# Revit family: Building-IEC309Connections-GEWISS-IEC309HP-10°_FLUSH-MOUNT_SOCKET_32A_IP44-54
name_source: partatom
category: Apparecchi elettrici
units: mm (PartAtom-declared; Revit-internal decimal feet)

## family parameters
Condiviso = Sì
Host = Superficie
Mantenere orientamento annotazione = Sì
Punto di calcolo locali = Sì
Quota connettore circolare = Usa diametro
Taglio con vuoti quando caricato = No
Tipo di parte = Normale

## types (28) — shared parameters
Breaking capacity at 1.1 Un = 40A
Catalogue = BUILDING
Corpo centrale = Default(2)
FORMULA = 1000 mm  [stored 3.28084 ft]
Flange dimensions (mm) = 95x80
Glow wire test: = 850 °C (active parts) - 650 °C (passive parts)
IDF = e593e5aa-3fae-48bf-b1cb-87c0f69a9db0
IDT = b8406758f3304951a22d0997e08313ec
IP degree = IP44/IP54
Immagine tipo = <Nessuno>
Insulation resistance = - 10 M?
L = 155 mm  [stored 0.50853 ft]
Operating temperature: = -25 +55 °C
Permissible overload = 42A
Piastra = Default(2)
Produttore = GEWISS S.p.A.
Prospetto di default = 500 mm  [stored 1.64042 ft]
Rated current (A) = 32
SEO = Socket outlet
SPinotto = Default(2)
Shock resistance = IK09
Sportello_visibile = Sì
Spostamento_S = 960 mm
Technical sheet = https://www.gewiss.com
Terminal tightening capacity = 2.5-6mm² flexible cables - 2.5-10mm² rigid cables
Thermo-pressure with ball = 125 °C (active parts) - 80 °C (passive parts)
Total number of operations = -2000
Type of material = Halogen-free in compliance with EN 60754-2
Type of wiring = With screw
Typology = 10° angled flush-mounting socket-outlet
URL = https://www.gewiss.com
Version file RFA = 21.11
W = 115 mm  [stored 0.377297 ft]

## per-type parameters (varying)
| type | Colour: | Descrizione | Electrocod | Frequency | Modello | No. of poles | Rated voltage: | Reference h |
| GW62219H - 10°FLUSH.S.O.  HP IP44 2P+E 32A 400V 9H | Red | 10°FLUSH.S.O.  HP IP44 2P+E 32A 400V 9H | 2210 | 50/60 Hz | GW62219H | 2P+E | 380 - 415 V | 9 |
| GW62832H - 10°FLUSH.S.O. HP IP44 3P+E 32A TRASF.12H | Grey | 10°FLUSH.S.O. HP IP44 3P+E 32A TRASF.12H | 2211 | 50/60 Hz | GW62832H | 3P+E | transf. | 12 |
| GW62831H - 10°FLUSH.S.O. HP IP44 2P+E 32A TRASF.12H | Grey | 10°FLUSH.S.O. HP IP44 2P+E 32A TRASF.12H | 2211 | 50/60 Hz | GW62831H | 2P+E | transf. | 12 |
| GW62820H - 10°FLUSH.S.O. HP IP44 3P+N+E 32A 690V 5H | Black | 10°FLUSH.S.O. HP IP44 3P+N+E 32A 690V 5H | 2211 | 50/60 Hz | GW62820H | 3P+N+E | 600 - 690 V | 5 |
| GW62834H - 10°FLUSH.S.O. HP IP44 2P+E 32A-250Vcc8H | Grey | 10°FLUSH.S.O. HP IP44 2P+E 32A >250Vcc8H | 2211 | d.c. | GW62834H | 2P+E | -250 V | 8 |
| GW62826H - 10°FLUSH.S.O.  HP IP44 3P+N+E 32A-50V2H | Green | 10°FLUSH.S.O.  HP IP44 3P+N+E 32A >50V2H | 2211 | -300 - 500 Hz | GW62826H | 3P+N+E | -50 V | 2 |
| GW62822H - 10°FLUSH.S.O.  HP IP44 3P+E 32A-50V 10H | Green | 10°FLUSH.S.O.  HP IP44 3P+E 32A >50V 10H | 2211 | 100 - 300 Hz | GW62822H | 3P+E | -50 V | 10 |
| GW62830H - 10°FL.S.O. HP IP44 3P+N+E 32A 380/440V3H | Red | 10°FL.S.O. HP IP44 3P+N+E 32A 380/440V3H | 2211 | 50/60 Hz | GW62830H | 3P+N+E | 380 - 440 V | 3 |
| GW62819H - 10°FLUSH.S.O.  HP IP44 3P+E 32A 690V 5H | Black | 10°FLUSH.S.O.  HP IP44 3P+E 32A 690V 5H | 2211 | 50/60 Hz | GW62819H | 3P+E | 600 - 690 V | 5 |
| GW62821H - 10°FLUSH.S.O.  HP IP44 2P+E 32A-50V 10H | Green | 10°FLUSH.S.O.  HP IP44 2P+E 32A >50V 10H | 2211 | 100 - 300 Hz | GW62821H | 2P+E | -50 V | 10 |
| GW62217H - 10°FLUSH.S.O.  HP IP44 3P+E 32A 230V 9H | Blue | 10°FLUSH.S.O.  HP IP44 3P+E 32A 230V 9H | 2210 | 50/60 Hz | GW62217H | 3P+E | 200 - 250 V | 9 |
| GW62214H - 10°FLUSH.S.O.  HP IP44 3P+E 32A 110V 4H | Yellow | 10°FLUSH.S.O.  HP IP44 3P+E 32A 110V 4H | 2210 | 50/60 Hz | GW62214H | 3P+E | 100 - 130 V | 4 |
| GW62216H - 10°FLUSH.S.O.  HP IP44 2P+E 32A 230V 6H | Blue | 10°FLUSH.S.O.  HP IP44 2P+E 32A 230V 6H | 2210 | 50/60 Hz | GW62216H | 2P+E | 200 - 250 V | 6 |
| GW62220H - 10°FLUSH.S.O.  HP IP44 3P+E 32A 400V 6H | Red | 10°FLUSH.S.O.  HP IP44 3P+E 32A 400V 6H | 2210 | 50/60 Hz | GW62220H | 3P+E | 380 - 415 V | 6 |
| GW62223H - 10°FLUSH.S.O. HP IP44 3P+N+E 32A 500V 7H | Black | 10°FLUSH.S.O. HP IP44 3P+N+E 32A 500V 7H | 2210 | 50/60 Hz | GW62223H | 3P+N+E | 480 - 500 V | 7 |
| GW62824H - 10°FLUSH.S.O.  HP IP44 2P+E 32A-50V 2H | Green | 10°FLUSH.S.O.  HP IP44 2P+E 32A >50V 2H | 2211 | -300 - 500 Hz | GW62824H | 2P+E | -50 V | 2 |
| GW62218H - 10°FLUSH.S.O. HP IP44 3P+N+E 32A 230V 9H | Blue | 10°FLUSH.S.O. HP IP44 3P+N+E 32A 230V 9H | 2210 | 50/60 Hz | GW62218H | 3P+N+E | 200 - 250 V | 9 |
| GW62829H - 10°FL.S.O. HP IP44 3P+E 32A 380/440V 3H | Red | 10°FL.S.O. HP IP44 3P+E 32A 380/440V 3H | 2211 | 50/60 Hz | GW62829H | 3P+E | 380 - 440 V | 3 |
| GW62221H - 10°FLUSH.S.O. HP IP44 3P+N+E 32A 400V 6H | Red | 10°FLUSH.S.O. HP IP44 3P+N+E 32A 400V 6H | 2210 | 50/60 Hz | GW62221H | 3P+N+E | 380 - 415 V | 6 |
| GW62833H - 10°FL.S.O. HP IP44 2P+E 32A-50÷250Vcc3H | Grey | 10°FL.S.O. HP IP44 2P+E 32A >50÷250Vcc3H | 2211 | d.c. | GW62833H | 2P+E | -50 - 250 V | 3 |
| GW62825H - 10°FLUSH.S.O.  HP IP44 3P+E 32A-50V 2H | Green | 10°FLUSH.S.O.  HP IP44 3P+E 32A >50V 2H | 2211 | -300 - 500 Hz | GW62825H | 3P+E | -50 V | 2 |
| GW62823H - 10°FLUSH.S.O. HP IP44 3P+N+E 32A-50V10H | Green | 10°FLUSH.S.O. HP IP44 3P+N+E 32A >50V10H | 2211 | 100 - 300 Hz | GW62823H | 3P+N+E | -50 V | 10 |
| GW62828H - 10°FL.S.O.HP IP44 3P+N+E 32A 440÷460V11H | Red | 10°FL.S.O.HP IP44 3P+N+E 32A 440÷460V11H | 2211 | 60 Hz | GW62828H | 3P+N+E | 440 - 460 V | 11 |
| GW62818H - 10°FLUSH.S.O.  HP IP44 2P+E 32A 500V 7H | Black | 10°FLUSH.S.O.  HP IP44 2P+E 32A 500V 7H | 2211 | 50/60 Hz | GW62818H | 2P+E | 480 - 500 V | 7 |
| GW62215H - 10°FLUSH.S.O. HP IP44 3P+N+E 32A 110V 4H | Yellow | 10°FLUSH.S.O. HP IP44 3P+N+E 32A 110V 4H | 2210 | 50/60 Hz | GW62215H | 3P+N+E | 100 - 130 V | 4 |
| GW62222H - 10°FLUSH.S.O.  HP IP44 3P+E 32A 500V 7H | Black | 10°FLUSH.S.O.  HP IP44 3P+E 32A 500V 7H | 2210 | 50/60 Hz | GW62222H | 3P+E | 480 - 500 V | 7 |
| GW62827H - 10°FL.S.O. HP IP44 3P+E 32A 440÷460V11H | Red | 10°FL.S.O. HP IP44 3P+E 32A 440÷460V11H | 2211 | 60 Hz | GW62827H | 3P+E | 440 - 460 V | 11 |
| GW62213H - 10°FLUSH.S.O.  HP IP44 2P+E 32A 110V 4H | Yellow | 10°FLUSH.S.O.  HP IP44 2P+E 32A 110V 4H | 2210 | 50/60 Hz | GW62213H | 2P+E | 100 - 130 V | 4 |

note: [stored X ft] marks values corroborated as IEEE doubles in the binary element streams (Revit-internal decimal feet)

## geometry (parser evidence)
native form markers: Sweep x2
no freeform markers — native parametric forms only
